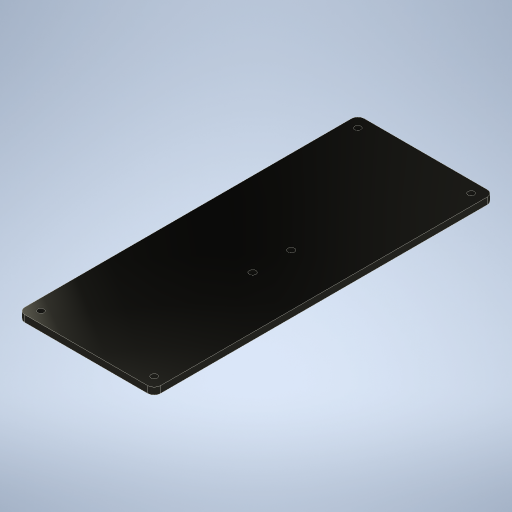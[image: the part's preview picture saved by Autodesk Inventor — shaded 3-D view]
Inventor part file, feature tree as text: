
AUTODESK INVENTOR PART (.ipt)
format: ipt  version: 2023 (Build 270158000, 158)  size: 267,264 bytes
history: native  units: in
note: dims shown in document units (in); Inventor stores cm internally (conversion verified against a paired STEP export)
features: fillet x4, extrude x1, sketch x1
ambient origin geometry x8: Origin, YZ Plane, XZ Plane, XY Plane, X Axis, Y Axis, Z Axis, Center Point
bodies: Solid1 (feature_tree)
feature tree (6):
  extrude  "Extrusion1"  Depth=0.1181in TaperAngle=0.0deg
  fillet  "Fillet1"  Radius=0.1102in
  fillet  "Fillet2"  Radius=0.1102in
  fillet  "Fillet3"  Radius=0.1102in
  fillet  "Fillet4"  Radius=0.1102in
  sketch  "Sketch1"  dims[d0=2.3622in d1=5.9055in d2=0.1969in d3=0.1969in d4=0.1969in d5=0.1969in d6=0.1969in d8=0.1969in d10=0.1102in d11=0.1102in d12=0.7492in d13=0.8681in d14=0.0984in d15=0.0984in d16=0.0984in d17=0.0984in d18=0.1181in d19=0.1181in d20=0.0394in d21=0.1575in d41=0.1181in d42=0.0in d43=0.1102in d44=0.1102in d45=0.1102in d46=0.1102in]
